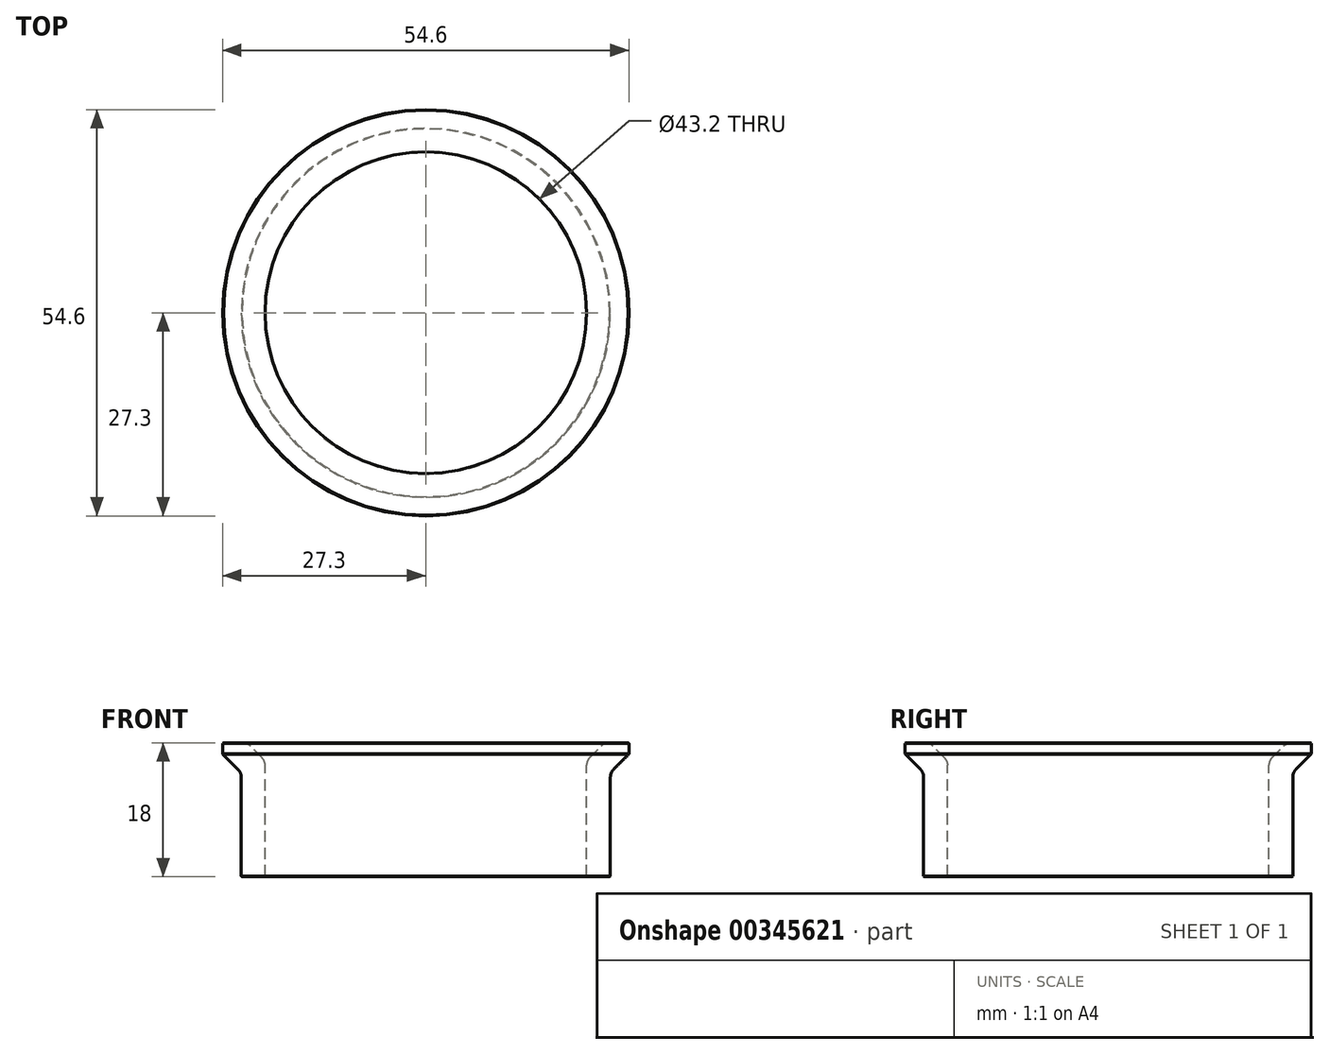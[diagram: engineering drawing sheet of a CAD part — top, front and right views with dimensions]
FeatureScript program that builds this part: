
annotation { "Feature Type Name" : "Feature", "Feature Type Description" : "" }
export const myFeature = defineFeature(function(context is Context, id is Id, definition is map)
    precondition{}
    {
        {
            var Q0;
            Q0=qCreatedBy(makeId("Front.planeOp"),FACE);
            var sketch = newSketch(context, id + "F0", { "sketchPlane" : qUnion([Q0])});
            skLineSegment(sketch, "E0", {"start": v(21.6, 0) * mm, "end": v(21.6, 15.6) * mm});
            skLineSegment(sketch, "E1", {"start": v(21.6, 15.6) * mm, "end": v(24, 18) * mm});
            skLineSegment(sketch, "E2", {"start": v(24, 18) * mm, "end": v(27.3, 18) * mm});
            skLineSegment(sketch, "E3", {"start": v(27.3, 18) * mm, "end": v(27.3, 0) * mm});
            skLineSegment(sketch, "E4", {"start": v(27.3, 0) * mm, "end": v(21.6, 0) * mm});
            skLineSegment(sketch, "E5", {"start": v(0, 34.4) * mm, "end": v(0, -22.39) * mm, "construction": true});
            skLineSegment(sketch, "E6", {"start": v(27.3, 16.5) * mm, "end": v(24.8, 14) * mm});
            skLineSegment(sketch, "E7", {"start": v(24.8, 14) * mm, "end": v(24.8, 0) * mm});
            skSolve(sketch);
        }
        {
            var Q0;
            {var subQ3=sQuery(id+"F0.wireOp",EDGE,"E0");Q0=makeQuery(id+"F0.imprint","IMPRINT",FACE,{"disambiguationData":[TD([[makeQuery(id+"F0.imprint","IMPRINT",EDGE,{"derivedFrom":subQ3}),-1.0]])]});}
            var Q1;
            Q1=sQuery(id+"F0.wireOp",EDGE,"E5");
            revolve(context, id + "F1", {"entities" : qUnion([Q0]), "axis" : qUnion([Q1]), "revolveType" : RevolveType.FULL});
        }
        {
            var Q0;
            Q0=makeQuery(id+"F1.opRevolve","SWEPT_EDGE",EDGE,{"disambiguationData":[OSD([sQuery(id+"F0.wireOp",EDGE,"E0"),sQuery(id+"F0.wireOp",EDGE,"E1")])]});
            fillet(context, id + "F2", {"entities" : qUnion([Q0]), "radius" : 1.5 * mm, "tangentPropagation" : true, "allowEdgeOverflow" : false});
        }
        {
            var Q0;
            Q0=makeQuery(id+"F1.opRevolve","SWEPT_EDGE",EDGE,{"disambiguationData":[OSD([sQuery(id+"F0.wireOp",EDGE,"E1"),sQuery(id+"F0.wireOp",EDGE,"E2")])]});
            fillet(context, id + "F3", {"entities" : qUnion([Q0]), "radius" : 1.5 * mm, "tangentPropagation" : true, "allowEdgeOverflow" : false});
        }
        {
            var Q0;
            Q0=makeQuery(id+"F1.opRevolve","SWEPT_EDGE",EDGE,{"disambiguationData":[OSD([sQuery(id+"F0.wireOp",EDGE,"E6"),sQuery(id+"F0.wireOp",EDGE,"E7")])]});
            fillet(context, id + "F4", {"entities" : qUnion([Q0]), "radius" : 1.5 * mm, "tangentPropagation" : true, "allowEdgeOverflow" : false});
        }
        {
            var Q0;
            Q0=makeQuery(id+"F1.opRevolve","SWEPT_EDGE",EDGE,{"disambiguationData":[OSD([sQuery(id+"F0.wireOp",EDGE,"E2"),sQuery(id+"F0.wireOp",EDGE,"E3")])]});
            var Q1;
            Q1=makeQuery(id+"F1.opRevolve","SWEPT_FACE",FACE,{"disambiguationData":[OSD([sQuery(id+"F0.wireOp",EDGE,"E3")])]});
            var Q2;
            Q2=makeQuery(id+"F1.opRevolve","SWEPT_EDGE",EDGE,{"disambiguationData":[OSD([sQuery(id+"F0.wireOp",EDGE,"E4"),sQuery(id+"F0.wireOp",EDGE,"E7")])]});
            var Q3;
            Q3=makeQuery(id+"F1.opRevolve","SWEPT_EDGE",EDGE,{"disambiguationData":[OSD([sQuery(id+"F0.wireOp",EDGE,"E0"),sQuery(id+"F0.wireOp",EDGE,"E4")])]});
            chamfer(context, id + "F5", {"entities" : qUnion([Q0, Q1, Q2, Q3]), "width" : 0.1 * mm, "tangentPropagation" : true});
        }
    });
